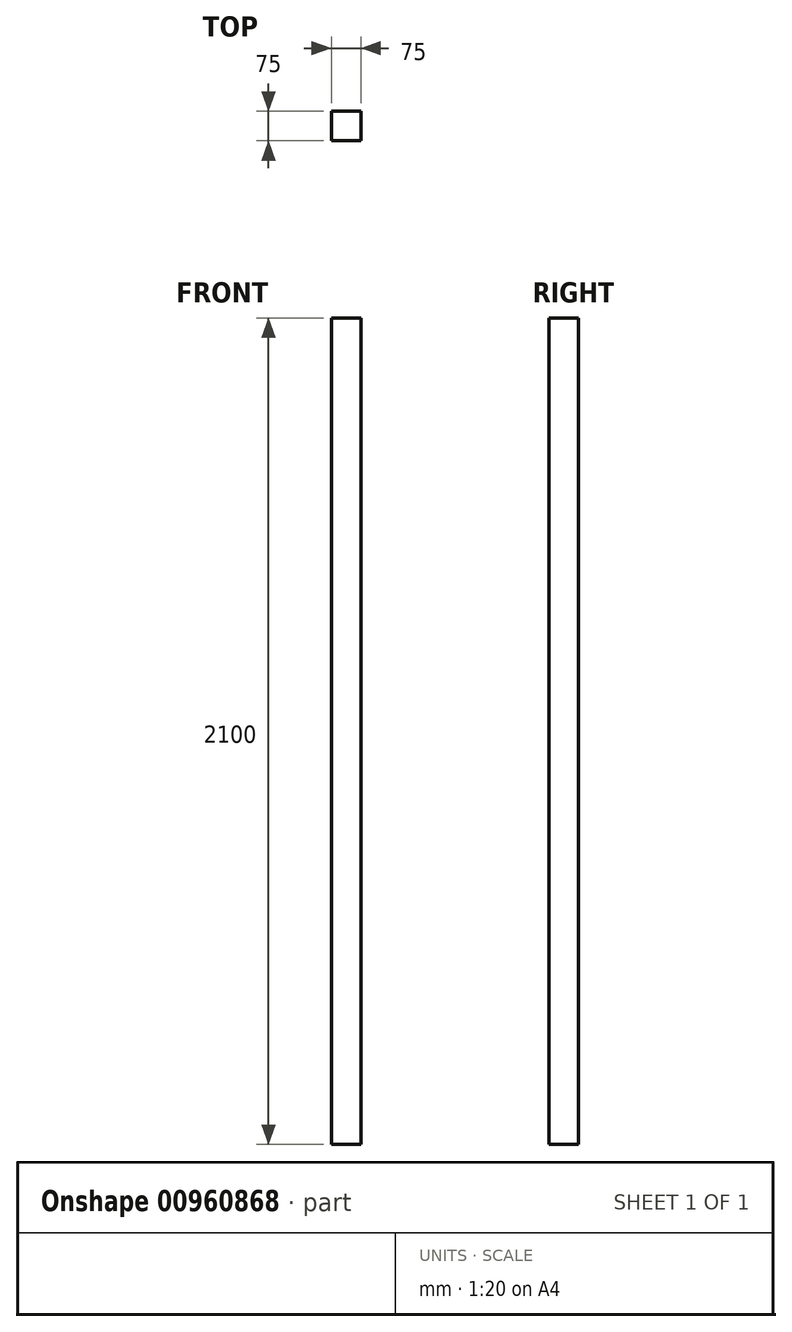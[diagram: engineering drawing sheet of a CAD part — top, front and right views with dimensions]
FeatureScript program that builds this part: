
annotation { "Feature Type Name" : "Feature", "Feature Type Description" : "" }
export const myFeature = defineFeature(function(context is Context, id is Id, definition is map)
    precondition{}
    {
        {
            var Q0;
            Q0=qCreatedBy(makeId("Top.planeOp"),FACE);
            var sketch = newSketch(context, id + "F0", { "sketchPlane" : qUnion([Q0])});
            skLineSegment(sketch, "E0.bottom", {"start": v(-182.02, 1.74) * mm, "end": v(-107.02, 1.74) * mm});
            skLineSegment(sketch, "E0.top", {"start": v(-182.02, -73.26) * mm, "end": v(-107.02, -73.26) * mm});
            skLineSegment(sketch, "E0.left", {"start": v(-182.02, 1.74) * mm, "end": v(-182.02, -73.26) * mm});
            skLineSegment(sketch, "E0.right", {"start": v(-107.02, 1.74) * mm, "end": v(-107.02, -73.26) * mm});
            skSolve(sketch);
        }
        {
            var Q0;
            Q0=makeQuery(id+"F0.imprint","IMPRINT",FACE,{"disambiguationData":[TD([[makeQuery(id+"F0.imprint","IMPRINT",EDGE,{"derivedFrom":sQuery(id+"F0.wireOp",EDGE,"E0.bottom")}),-1.0]])]});
            extrude(context, id + "F1", {"entities" : qUnion([Q0]), "depth" : 2100 * mm, "offsetDistance" : 25 * mm});
        }
    });
